FCSTD DOCUMENT  (FreeCAD 1.0R39319 (Git))
Label: Assembly
License: All rights reserved
objects: App::Link×22, App::FeaturePython×14, Assembly::JointGroup×1, Assembly::AssemblyObject×1
EXTERNAL_REF file=RuderlageV2.FCStd obj=Body
EXTERNAL_REF file=RuderlageV2.FCStd obj=Body012
EXTERNAL_REF file=RuderlageV2.FCStd obj=ThreadedRod
EXTERNAL_REF file=RuderlageV2.FCStd obj=Nut
EXTERNAL_REF file=RuderlageV2.FCStd obj=Washer
EXTERNAL_REF file=RuderlageV2.FCStd obj=Washer001
EXTERNAL_REF file=RuderlageV2.FCStd obj=Nut002
EXTERNAL_REF file=RuderlageV2.FCStd obj=Part
EXTERNAL_REF file=RuderlageV2.FCStd obj=Washer002
EXTERNAL_REF file=RuderlageV2.FCStd obj=Washer004
EXTERNAL_REF file=RuderlageV2.FCStd obj=Body018
EXTERNAL_REF file=RuderlageV2.FCStd obj=Washer005
EXTERNAL_REF file=RuderlageV2.FCStd obj=Washer008
EXTERNAL_REF file=RuderlageV2.FCStd obj=Washer009
EXTERNAL_REF file=RuderlageV2.FCStd obj=Washer010
EXTERNAL_REF file=RuderlageV2.FCStd obj=Washer011
EXTERNAL_REF file=RuderlageV2.FCStd obj=Nut007
EXTERNAL_REF file=RuderlageV2.FCStd obj=Nut008

FEATURE [App::Link] Montageplatte
  LinkPlacement = pos=(8.31309e-11,-1.38945e-10,0) rot=(0,0,-1;0.523599rad)
  LinkedObject = -> <external RuderlageV2.FCStd>#Body
  Placement = pos=(8.31309e-11,-1.38945e-10,0) rot=(0,0,-1;0.523599rad)
FEATURE [App::Link] Montageplatte1
  LinkedObject = -> <external RuderlageV2.FCStd>#Body012
FEATURE [App::FeaturePython] GroundedJoint  # Assembly grounded joint (typed FeaturePython)
  ObjectToGround = -> Montageplatte1
FEATURE [App::Link] M5x48_ThreadedRod  label="M5x48-ThreadedRod"
  LinkPlacement = pos=(16.0215,-9.25,48) rot=(0,0,-1;0.523599rad)
  LinkedObject = -> <external RuderlageV2.FCStd>#ThreadedRod
  Placement = pos=(16.0215,-9.25,48) rot=(0,0,-1;0.523599rad)
FEATURE [App::Link] M5x48_ThreadedRod001  label="M5x48-ThreadedRod001"
  LinkPlacement = pos=(-16.0215,9.25,48) rot=(0,0,-1;0.523599rad)
  LinkedObject = -> <external RuderlageV2.FCStd>#ThreadedRod
  Placement = pos=(-16.0215,9.25,48) rot=(0,0,-1;0.523599rad)
FEATURE [App::Link] M5_Nut  label="M5-Nut"
  LinkPlacement = pos=(-16.0215,9.25,9.5) rot=(0,0,-1;0.523599rad)
  LinkedObject = -> <external RuderlageV2.FCStd>#Nut
  Placement = pos=(-16.0215,9.25,9.5) rot=(0,0,-1;0.523599rad)
FEATURE [App::Link] M5_Nut001  label="M5-Nut001"
  LinkPlacement = pos=(16.0215,-9.25,9.5) rot=(0,0,-1;0.523599rad)
  LinkedObject = -> <external RuderlageV2.FCStd>#Nut
  Placement = pos=(16.0215,-9.25,9.5) rot=(0,0,-1;0.523599rad)
FEATURE [App::Link] M5_Washer  label="M5-Washer"
  LinkPlacement = pos=(16.0215,-9.25,5) rot=(0,0,-1;0.523599rad)
  LinkedObject = -> <external RuderlageV2.FCStd>#Washer
  Placement = pos=(16.0215,-9.25,5) rot=(0,0,-1;0.523599rad)
FEATURE [App::Link] M5_Washer001  label="M5-Washer001"
  LinkPlacement = pos=(-16.0215,9.25,5) rot=(0,0,-1;0.523599rad)
  LinkedObject = -> <external RuderlageV2.FCStd>#Washer001
  Placement = pos=(-16.0215,9.25,5) rot=(0,0,-1;0.523599rad)
FEATURE [App::Link] M5_Nut007  label="M5-Nut007"
  LinkPlacement = pos=(-16.0215,9.25,6) rot=(0,0,-1;0.523599rad)
  LinkedObject = -> <external RuderlageV2.FCStd>#Nut002
  Placement = pos=(-16.0215,9.25,6) rot=(0,0,-1;0.523599rad)
FEATURE [App::Link] Sensor
  LinkPlacement = pos=(25.067,-84.0879,-19.1551) rot=(0,0,1;1.28251rad)
  LinkedObject = -> <external RuderlageV2.FCStd>#Part
  Placement = pos=(25.067,-84.0879,-19.1551) rot=(0,0,1;1.28251rad)
FEATURE [App::Link] M5_Nut008  label="M5-Nut008"
  LinkPlacement = pos=(16.0215,-9.25,6) rot=(0,0,-1;0.523599rad)
  LinkedObject = -> <external RuderlageV2.FCStd>#Nut002
  Placement = pos=(16.0215,-9.25,6) rot=(0,0,-1;0.523599rad)
FEATURE [App::Link] M5_Washer002  label="M5-Washer002"
  LinkPlacement = pos=(16.0215,-9.25,13) rot=(0,0,-1;0.523599rad)
  LinkedObject = -> <external RuderlageV2.FCStd>#Washer002
  Placement = pos=(16.0215,-9.25,13) rot=(0,0,-1;0.523599rad)
FEATURE [App::Link] M5_Washer004  label="M5-Washer004"
  LinkPlacement = pos=(-16.0215,9.25,13) rot=(0,0,-1;0.523599rad)
  LinkedObject = -> <external RuderlageV2.FCStd>#Washer004
  Placement = pos=(-16.0215,9.25,13) rot=(0,0,-1;0.523599rad)
FEATURE [App::Link] MotherBoard
  LinkedObject = -> <external RuderlageV2.FCStd>#Body018
FEATURE [App::Link] M5_Washer005  label="M5-Washer005"
  LinkPlacement = pos=(-7.32401,-18.5886,24.9799) rot=(0,0,1;3.66519rad)
  LinkedObject = -> <external RuderlageV2.FCStd>#Washer004
  Placement = pos=(-7.32401,-18.5886,24.9799) rot=(0,0,1;3.66519rad)
FEATURE [App::Link] M5_Washer006  label="M5-Washer006"
  LinkPlacement = pos=(4.68514,-9.73796,41.904) rot=(0,0,1;0.523599rad)
  LinkedObject = -> <external RuderlageV2.FCStd>#Washer005
  Placement = pos=(4.68514,-9.73796,41.904) rot=(0,0,1;0.523599rad)
FEATURE [App::Link] M5_Washer007  label="M5-Washer007"
  LinkPlacement = pos=(45.8554,-53.5845,20.7119) rot=(0,0,1;4.42411rad)
  LinkedObject = -> <external RuderlageV2.FCStd>#Washer008
  Placement = pos=(45.8554,-53.5845,20.7119) rot=(0,0,1;4.42411rad)
FEATURE [App::Link] M5_Washer008  label="M5-Washer008"
  LinkPlacement = pos=(11.8704,-37.3648,8.91253) rot=(0,0,1;1.28251rad)
  LinkedObject = -> <external RuderlageV2.FCStd>#Washer009
  Placement = pos=(11.8704,-37.3648,8.91253) rot=(0,0,1;1.28251rad)
FEATURE [App::Link] M5_Washer009  label="M5-Washer009"
  LinkPlacement = pos=(14.8535,-31.465,16.0747) rot=(0,0,1;1.28251rad)
  LinkedObject = -> <external RuderlageV2.FCStd>#Washer010
  Placement = pos=(14.8535,-31.465,16.0747) rot=(0,0,1;1.28251rad)
FEATURE [App::Link] M5_Washer010  label="M5-Washer010"
  LinkPlacement = pos=(25.6315,-40.577,26.4909) rot=(0,0,1;1.28251rad)
  LinkedObject = -> <external RuderlageV2.FCStd>#Washer011
  Placement = pos=(25.6315,-40.577,26.4909) rot=(0,0,1;1.28251rad)
FEATURE [App::Link] M5_Nut014  label="M5-Nut014"
  LinkPlacement = pos=(22.6339,-41.8637,9.14513) rot=(0,0,1;1.28251rad)
  LinkedObject = -> <external RuderlageV2.FCStd>#Nut007
  Placement = pos=(22.6339,-41.8637,9.14513) rot=(0,0,1;1.28251rad)
FEATURE [App::Link] M5_Nut015  label="M5-Nut015"
  LinkPlacement = pos=(45.7753,-44.5792,32.2312) rot=(0,0,1;4.42411rad)
  LinkedObject = -> <external RuderlageV2.FCStd>#Nut008
  Placement = pos=(45.7753,-44.5792,32.2312) rot=(0,0,1;4.42411rad)
FEATURE [App::FeaturePython] Joint  label="Revolute"  # Assembly joint (typed FeaturePython)
  Activated = true
  AngleMax = 0
  AngleMin = 0
  Detach1 = false
  Detach2 = false
  Distance = 0
  Distance2 = 0
  EnableAngleMax = false
  EnableAngleMin = false
  EnableLengthMax = false
  EnableLengthMin = false
  JointType = 1 (Revolute)
  LengthMax = 0
  LengthMin = 0
  Placement1 = pos=(-8.72817e-11,-1.54759e-11,0) rot=(0,0,1;0rad)
  Placement2 = pos=(-1.952e-13,-3.03e-14,0) rot=(0,0,1;0rad)
  Reference1 = -> Assembly [Montageplatte.Edge2,Montageplatte.Edge2]
  Reference2 = -> Assembly [Montageplatte1.Edge2,Montageplatte1.Edge2]
FEATURE [App::FeaturePython] Joint001  label="Fixed"  # Assembly joint (typed FeaturePython)
  Activated = true
  AngleMax = 0
  AngleMin = 0
  Detach1 = false
  Detach2 = false
  Distance = 0
  Distance2 = 0
  EnableAngleMax = false
  EnableAngleMin = false
  EnableLengthMax = false
  EnableLengthMin = false
  JointType = 0 (Fixed)
  LengthMax = 0
  LengthMin = 0
  Placement1 = pos=(15.375,26.6303,0) rot=(0,0,1;0rad)
  Placement2 = pos=(2.63395e-11,30.75,0) rot=(0,0,1;0rad)
  Reference1 = -> Assembly [Montageplatte1.Edge10,Montageplatte1.Edge10]
  Reference2 = -> Assembly [Montageplatte.Edge17,Montageplatte.Edge17]
FEATURE [App::FeaturePython] Joint002  label="Fixed001"  # Assembly joint (typed FeaturePython)
  Activated = true
  AngleMax = 0
  AngleMin = 0
  Detach1 = false
  Detach2 = false
  Distance = 0
  Distance2 = 0
  EnableAngleMax = false
  EnableAngleMin = false
  EnableLengthMax = false
  EnableLengthMin = false
  JointType = 0 (Fixed)
  LengthMax = 0
  LengthMin = 0
  Placement1 = pos=(0,0,-48) rot=(0,0,1;0rad)
  Placement2 = pos=(-18.5,-4.081e-13,0) rot=(0,0,1;0rad)
  Reference1 = -> Assembly [M5x48_ThreadedRod001.Edge6,M5x48_ThreadedRod001.Edge6]
  Reference2 = -> Assembly [Montageplatte.Edge29,Montageplatte.Edge29]
FEATURE [App::FeaturePython] Joint003  label="Fixed002"  # Assembly joint (typed FeaturePython)
  Activated = true
  AngleMax = 0
  AngleMin = 0
  Detach1 = false
  Detach2 = false
  Distance = 0
  Distance2 = 0
  EnableAngleMax = false
  EnableAngleMin = false
  EnableLengthMax = false
  EnableLengthMin = false
  JointType = 0 (Fixed)
  LengthMax = 0
  LengthMin = 0
  Placement1 = pos=(18.5,-2.90021e-11,0) rot=(0,0,1;0rad)
  Placement2 = pos=(0,0,-48) rot=(0,0,1;0rad)
  Reference1 = -> Assembly [Montageplatte.Edge26,Montageplatte.Edge26]
  Reference2 = -> Assembly [M5x48_ThreadedRod.Edge6,M5x48_ThreadedRod.Edge6]
FEATURE [App::FeaturePython] Joint004  label="Fixed003"  # Assembly joint (typed FeaturePython)
  Activated = true
  AngleMax = 0
  AngleMin = 0
  Detach1 = false
  Detach2 = false
  Distance = 0
  Distance2 = 0
  EnableAngleMax = false
  EnableAngleMin = false
  EnableLengthMax = false
  EnableLengthMin = false
  JointType = 0 (Fixed)
  LengthMax = 0
  LengthMin = 0
  Placement2 = pos=(-18.5,-4.081e-13,5) rot=(0,0,1;0rad)
  Reference1 = -> Assembly [M5_Washer001.Edge5,M5_Washer001.Edge5]
  Reference2 = -> Assembly [Montageplatte.Edge30,Montageplatte.Edge30]
FEATURE [App::FeaturePython] Joint005  label="Fixed004"  # Assembly joint (typed FeaturePython)
  Activated = true
  AngleMax = 0
  AngleMin = 0
  Detach1 = false
  Detach2 = false
  Distance = 0
  Distance2 = 0
  EnableAngleMax = false
  EnableAngleMin = false
  EnableLengthMax = false
  EnableLengthMin = false
  JointType = 0 (Fixed)
  LengthMax = 0
  LengthMin = 0
  Placement2 = pos=(0,0,1) rot=(0,0,1;0rad)
  Reference1 = -> Assembly [M5_Nut007.Edge27,M5_Nut007.Edge27]
  Reference2 = -> Assembly [M5_Washer001.Edge1,M5_Washer001.Edge1]
FEATURE [App::FeaturePython] Joint006  label="Fixed005"  # Assembly joint (typed FeaturePython)
  Activated = true
  AngleMax = 0
  AngleMin = 0
  Detach1 = false
  Detach2 = false
  Distance = 0
  Distance2 = 0
  EnableAngleMax = false
  EnableAngleMin = false
  EnableLengthMax = false
  EnableLengthMin = false
  JointType = 0 (Fixed)
  LengthMax = 0
  LengthMin = 0
  Placement2 = pos=(0,0,3.5) rot=(0,0,1;0rad)
  Reference1 = -> Assembly [M5_Nut.Edge27,M5_Nut.Edge27]
  Reference2 = -> Assembly [M5_Nut007.Edge2,M5_Nut007.Edge2]
FEATURE [App::FeaturePython] Joint007  label="Fixed006"  # Assembly joint (typed FeaturePython)
  Activated = true
  AngleMax = 0
  AngleMin = 0
  Detach1 = false
  Detach2 = false
  Distance = 0
  Distance2 = 0
  EnableAngleMax = false
  EnableAngleMin = false
  EnableLengthMax = false
  EnableLengthMin = false
  JointType = 0 (Fixed)
  LengthMax = 0
  LengthMin = 0
  Placement2 = pos=(0,0,3.5) rot=(0,0,1;0rad)
  Reference1 = -> Assembly [M5_Washer004.Edge5,M5_Washer004.Edge5]
  Reference2 = -> Assembly [M5_Nut.Edge2,M5_Nut.Edge2]
FEATURE [App::FeaturePython] Joint008  label="Fixed007"  # Assembly joint (typed FeaturePython)
  Activated = true
  AngleMax = 0
  AngleMin = 0
  Detach1 = false
  Detach2 = false
  Distance = 0
  Distance2 = 0
  EnableAngleMax = false
  EnableAngleMin = false
  EnableLengthMax = false
  EnableLengthMin = false
  JointType = 0 (Fixed)
  LengthMax = 0
  LengthMin = 0
  Placement2 = pos=(18.5,-2.90021e-11,5) rot=(0,0,1;0rad)
  Reference1 = -> Assembly [M5_Washer.Edge5,M5_Washer.Edge5]
  Reference2 = -> Assembly [Montageplatte.Edge27,Montageplatte.Edge27]
FEATURE [App::FeaturePython] Joint009  label="Fixed008"  # Assembly joint (typed FeaturePython)
  Activated = true
  AngleMax = 0
  AngleMin = 0
  Detach1 = false
  Detach2 = false
  Distance = 0
  Distance2 = 0
  EnableAngleMax = false
  EnableAngleMin = false
  EnableLengthMax = false
  EnableLengthMin = false
  JointType = 0 (Fixed)
  LengthMax = 0
  LengthMin = 0
  Placement2 = pos=(0,0,1) rot=(0,0,1;0rad)
  Reference1 = -> Assembly [M5_Nut008.Edge27,M5_Nut008.Edge27]
  Reference2 = -> Assembly [M5_Washer.Edge1,M5_Washer.Edge1]
FEATURE [App::FeaturePython] Joint010  label="Fixed009"  # Assembly joint (typed FeaturePython)
  Activated = true
  AngleMax = 0
  AngleMin = 0
  Detach1 = false
  Detach2 = false
  Distance = 0
  Distance2 = 0
  EnableAngleMax = false
  EnableAngleMin = false
  EnableLengthMax = false
  EnableLengthMin = false
  JointType = 0 (Fixed)
  LengthMax = 0
  LengthMin = 0
  Placement1 = pos=(0,0,3.5) rot=(0,0,1;0rad)
  Reference1 = -> Assembly [M5_Nut008.Edge2,M5_Nut008.Edge2]
  Reference2 = -> Assembly [M5_Nut001.Edge27,M5_Nut001.Edge27]
FEATURE [App::FeaturePython] Joint011  label="Fixed010"  # Assembly joint (typed FeaturePython)
  Activated = true
  AngleMax = 0
  AngleMin = 0
  Detach1 = false
  Detach2 = false
  Distance = 0
  Distance2 = 0
  EnableAngleMax = false
  EnableAngleMin = false
  EnableLengthMax = false
  EnableLengthMin = false
  JointType = 0 (Fixed)
  LengthMax = 0
  LengthMin = 0
  Placement1 = pos=(0,0,3.5) rot=(0,0,1;0rad)
  Reference1 = -> Assembly [M5_Nut001.Edge2,M5_Nut001.Edge2]
  Reference2 = -> Assembly [M5_Washer002.Edge5,M5_Washer002.Edge5]
FEATURE [App::FeaturePython] Joint012  label="Parallel"  # Assembly joint (typed FeaturePython)
  Activated = true
  AngleMax = 0
  AngleMin = 0
  Detach1 = false
  Detach2 = false
  Distance = 0
  Distance2 = 0
  EnableAngleMax = false
  EnableAngleMin = false
  EnableLengthMax = false
  EnableLengthMin = false
  JointType = 6 (Parallel)
  LengthMax = 0
  LengthMin = 0
  Placement1 = pos=(0,-1.8e-15,1) rot=(0,1,0;3.14159rad)
  Placement2 = pos=(0,-18.5,0) rot=(0,0,1;0rad)
  Reference1 = -> Assembly [M5_Washer004.Face1,M5_Washer004.Face1]
  Reference2 = -> Assembly [MotherBoard.Face10,MotherBoard.Edge4]
FEATURE [Assembly::JointGroup] Joints
  Group = -> [GroundedJoint,Joint,Joint001,Joint002,Joint003,Joint004,Joint005,Joint006,Joint007,Joint008,Joint009,Joint010,Joint011,Joint012]
FEATURE [Assembly::AssemblyObject] Assembly
  Group = -> [Joints,Montageplatte,Montageplatte1,GroundedJoint,M5x48_ThreadedRod,M5x48_ThreadedRod001,M5_Nut,M5_Nut001,M5_Washer,M5_Washer001,M5_Nut007,Sensor,M5_Nut008,M5_Washer002,M5_Washer004,MotherBoard,M5_Washer005,M5_Washer006,M5_Washer007,M5_Washer008,M5_Washer009,M5_Washer010,M5_Nut014,M5_Nut015,Joint,Joint001,Joint002,Joint003,Joint004,Joint005,Joint006,Joint007,Joint008,Joint009,Joint010,Joint011,+1 more]
  Origin = -> Origin
  Type = Assembly

RESOLVED EXTERNAL PARTS (link-assembly join: the EXTERNAL_REF files above that resolve inside this repo's crawl, each included once):
---- part RuderlageV2.FCStd = doc fcstd_e4db90ef9637 (51563 chars; too large to inline — full recipe in that document) ----
